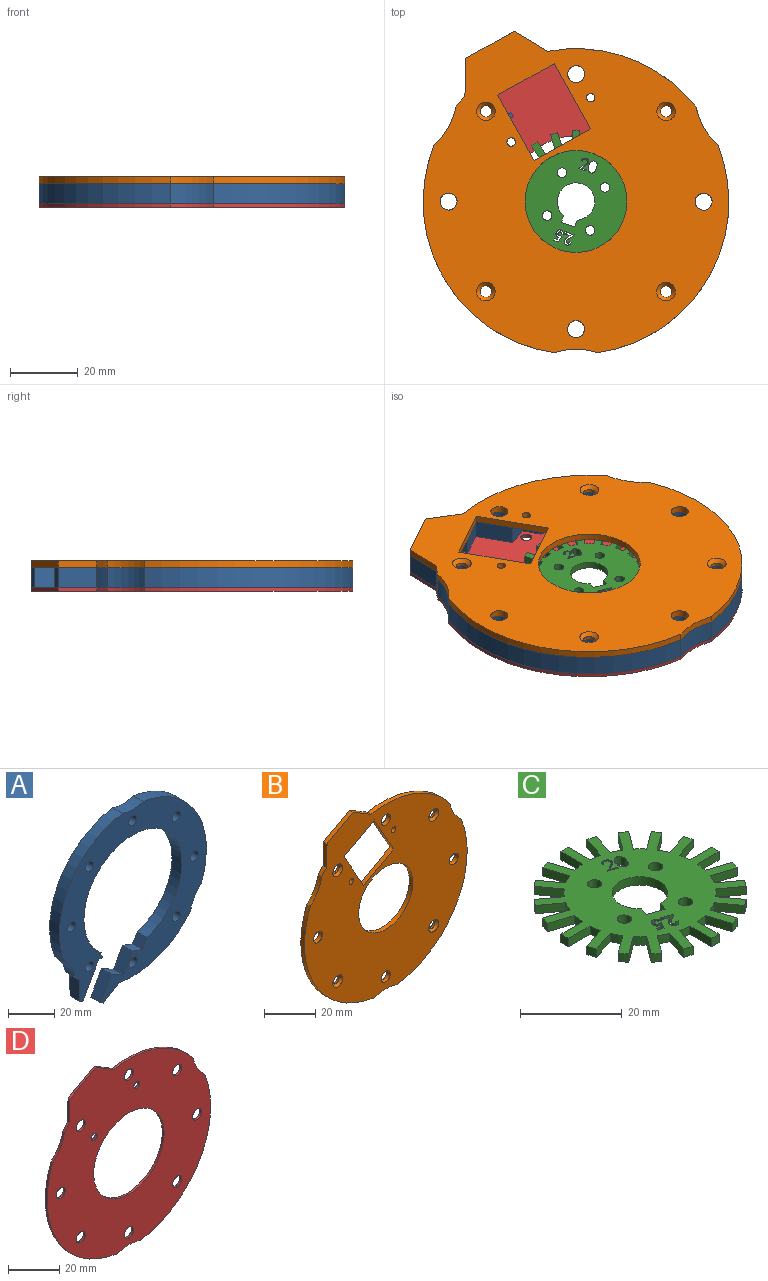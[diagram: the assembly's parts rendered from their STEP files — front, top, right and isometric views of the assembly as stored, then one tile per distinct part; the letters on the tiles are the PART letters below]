
ASSEMBLY  parts=4 mates=5
PART A: 32 faces, bbox 90x6x94.7 mm
  f0: cylinder r=20mm len=11.05mm, axis (0,1,0), area 77.9mm2, adj f1,f21,f22,f23
  f1: cylinder r=45mm len=6mm, axis (0,1,0), area 24.6mm2, adj f0,f2,f22,f23
  f2: plane 11.27x6mm, normal (-1,0,-0.02), area 67.6mm2, adj f1,f3,f22,f23
  f3: plane 6x1.75mm, normal (-0.48,0,-0.88), area 12mm2, adj f2,f4,f22,f23
  f4: plane 17.86x9.86mm, normal (0.88,0,-0.48), area 122.4mm2, adj f3,f5,f22,f23
  f5: plane 6x1.7mm, normal (-0.48,0,-0.88), area 11.6mm2, adj f4,f6,f22,f23
  f6: plane 6x1.23mm, normal (0.88,0,-0.48), area 8.4mm2, adj f5,f7,f22,f23
  f7: plane 6x1.7mm, normal (0.48,0,0.88), area 11.6mm2, adj f6,f8,f22,f23
  f8: plane 6x1.27mm, normal (0.88,0,-0.48), area 8.7mm2, adj f7,f9,f22,f23
  f9: cylinder r=30mm len=60mm, axis (0,1,0), area 951.8mm2, adj f8,f10,f22,f23
  f10: plane 6x4.97mm, normal (-0.88,0,0.48), area 34.1mm2, adj f9,f11,f22,f23
  f11: plane 6.17x6mm, normal (0.34,0,0.94), area 39.5mm2, adj f10,f12,f22,f23
  f12: plane 9.9x6mm, normal (-0.88,0,0.48), area 67.9mm2, adj f11,f13,f22,f23
  f13: plane 7.39x6mm, normal (0.48,0,0.88), area 50.7mm2, adj f12,f14,f22,f23
  f14: plane 11.91x6.57mm, normal (-0.88,0,0.48), area 81.6mm2, adj f13,f15,f22,f23
  f15: plane 6x1.75mm, normal (-0.48,0,-0.88), area 12mm2, adj f14,f16,f22,f23
  f16: plane 9.82x6mm, normal (0.52,0,-0.86), area 68.8mm2, adj f15,f17,f22,f23
  f17: cylinder r=45mm len=43.66mm, axis (0,1,0), area 294.3mm2, adj f16,f18,f22,f23
  f18: cylinder r=20mm len=11.06mm, axis (0,1,0), area 77.9mm2, adj f17,f19,f22,f23
  f19: cylinder r=45mm len=61.26mm, axis (0,1,0), area 488.7mm2, adj f18,f20,f22,f23
  f20: cylinder r=20mm len=12.76mm, axis (0,1,0), area 77.9mm2, adj f19,f21,f22,f23
  f21: cylinder r=45mm len=61.32mm, axis (0,1,0), area 488.7mm2, adj f0,f20,f22,f23
  f22: plane 94.71x90mm, normal (0,-1,0), area 3117.4mm2, adj f0,f1,f2,f3,f4,f5,f6,f7
  f23: plane 94.71x90mm, normal (0,1,0), area 3117.4mm2, adj f0,f1,f2,f3,f4,f5,f6,f7
  f24: cylinder r=2.5mm len=6mm, axis (0,1,0), area 94.2mm2, adj f22,f23
  f25: cylinder r=2.5mm len=6mm, axis (0,1,0), area 94.2mm2, adj f22,f23
  f26: cylinder r=2.5mm len=6mm, axis (0,1,0), area 94.2mm2, adj f22,f23
  f27: cylinder r=2.5mm len=6mm, axis (0,1,0), area 94.2mm2, adj f22,f23
  f28: cylinder r=2.5mm len=6mm, axis (0,1,0), area 94.2mm2, adj f22,f23
  f29: cylinder r=2.5mm len=6mm, axis (0,1,0), area 94.2mm2, adj f22,f23
  f30: cylinder r=2.5mm len=6mm, axis (0,1,0), area 94.2mm2, adj f22,f23
  f31: cylinder r=2.5mm len=6mm, axis (0,1,0), area 94.2mm2, adj f22,f23
PART B: 31 faces, bbox 90x2x94.7 mm
  f0: cylinder r=45mm len=61.29mm, axis (0,1,0), area 162.9mm2, adj f1,f9,f10,f11
  f1: cylinder r=20mm len=11.05mm, axis (0,1,0), area 26mm2, adj f0,f2,f10,f11
  f2: cylinder r=45mm len=43.67mm, axis (0,1,0), area 98.1mm2, adj f1,f3,f10,f11
  f3: plane 9.82x5.91mm, normal (0.52,0,0.86), area 22.9mm2, adj f2,f4,f10,f11
  f4: plane 14.4x7.96mm, normal (-0.48,0,0.88), area 32.9mm2, adj f3,f5,f10,f11
  f5: plane 11.27x2mm, normal (-1,0,0.02), area 22.5mm2, adj f4,f6,f10,f11
  f6: cylinder r=45mm len=3.11mm, axis (0,1,0), area 8.2mm2, adj f5,f7,f10,f11
  f7: cylinder r=20mm len=11.05mm, axis (0,1,0), area 26mm2, adj f6,f8,f10,f11
  f8: cylinder r=45mm len=61.29mm, axis (0,1,0), area 162.9mm2, adj f7,f9,f10,f11
  f9: cylinder r=20mm len=12.76mm, axis (0,1,0), area 26mm2, adj f0,f8,f10,f11
  f10: plane 94.69x90mm, normal (0,-1,0), area 5191.9mm2, adj f0,f1,f2,f3,f4,f5,f6,f7
  f11: plane 94.69x90mm, normal (0,1,0), area 5250.6mm2, adj f0,f1,f2,f3,f4,f5,f6,f7
  f12: cylinder r=15mm len=30mm, axis (0,1,0), area 188.5mm2, adj f10,f11
  f13: cylinder r=1.7mm len=3.4mm, axis (0,1,0), area 10.1mm2, adj f11,f30
  f14: cylinder r=1.7mm len=3.4mm, axis (0,1,0), area 10.1mm2, adj f11,f29
  f15: cylinder r=1.7mm len=3.4mm, axis (0,1,0), area 10.1mm2, adj f11,f28
  f16: cylinder r=2.5mm len=5mm, axis (0,1,0), area 31.4mm2, adj f10,f11
  f17: cylinder r=2.5mm len=5mm, axis (0,1,0), area 31.4mm2, adj f10,f11
  f18: cylinder r=1.7mm len=3.4mm, axis (0,1,0), area 10.1mm2, adj f11,f27
  f19: cylinder r=2.5mm len=5mm, axis (0,1,0), area 31.4mm2, adj f10,f11
  f20: cylinder r=2.5mm len=5mm, axis (0,1,0), area 31.4mm2, adj f10,f11
  f21: cylinder r=1.25mm len=2.5mm, axis (0,1,0), area 15.7mm2, adj f10,f11
  f22: cylinder r=1.25mm len=2.5mm, axis (0,1,0), area 15.7mm2, adj f10,f11
  f23: plane 19.23x10.69mm, normal (0.87,0,0.49), area 44mm2, adj f10,f11,f24,f26
  f24: plane 16.61x9.23mm, normal (-0.49,0,0.87), area 38mm2, adj f10,f11,f23,f25
  f25: plane 19.23x10.69mm, normal (-0.87,0,-0.49), area 44mm2, adj f10,f11,f24,f26
  f26: plane 16.61x9.23mm, normal (0.49,0,-0.87), area 38mm2, adj f10,f11,f23,f25
  f27: cone r=2.75mm half-angle=45deg, axis (0,-1,0), area 20.8mm2, adj f10,f18
  f28: cone r=2.75mm half-angle=45deg, axis (0,-1,0), area 20.8mm2, adj f10,f15
  f29: cone r=2.75mm half-angle=45deg, axis (0,-1,0), area 20.8mm2, adj f10,f14
  f30: cone r=2.75mm half-angle=45deg, axis (0,-1,0), area 20.8mm2, adj f10,f13
PART C: 138 faces, bbox 42x42x2 mm
  f0: plane 42x42mm, normal (0,0,-1), area 813.4mm2, adj f2,f3,f4,f5,f6,f7,f8,f9
  f1: plane 42x42mm, normal (0,0,1), area 813.4mm2, adj f2,f3,f4,f5,f6,f7,f8,f9
  f2: cylinder r=15mm len=2.58mm, axis (0,0,1), area 5.2mm2, adj f0,f1,f32,f87
  f3: cylinder r=15mm len=2.32mm, axis (0,0,1), area 5.2mm2, adj f0,f1,f84,f89
  f4: cylinder r=15mm len=2mm, axis (0,0,1), area 5.2mm2, adj f0,f1,f81,f86
  f5: cylinder r=15mm len=2.32mm, axis (0,0,1), area 5.2mm2, adj f0,f1,f78,f83
  f6: cylinder r=15mm len=2.58mm, axis (0,0,1), area 5.2mm2, adj f0,f1,f75,f80
  f7: cylinder r=15mm len=2.58mm, axis (0,0,1), area 5.2mm2, adj f0,f1,f72,f77
  f8: cylinder r=15mm len=2.32mm, axis (0,0,1), area 5.2mm2, adj f0,f1,f69,f74
  f9: cylinder r=15mm len=2mm, axis (0,0,1), area 5.2mm2, adj f0,f1,f66,f71
  f10: cylinder r=15mm len=2.32mm, axis (0,0,1), area 5.2mm2, adj f0,f1,f63,f68
  f11: cylinder r=15mm len=2.58mm, axis (0,0,1), area 5.2mm2, adj f0,f1,f60,f65
  f12: cylinder r=15mm len=2.58mm, axis (0,0,1), area 5.2mm2, adj f0,f1,f57,f62
  f13: cylinder r=15mm len=2.32mm, axis (0,0,1), area 5.2mm2, adj f0,f1,f54,f59
  f14: cylinder r=15mm len=2mm, axis (0,0,1), area 5.2mm2, adj f0,f1,f51,f56
  f15: cylinder r=15mm len=2.32mm, axis (0,0,1), area 5.2mm2, adj f0,f1,f48,f53
  f16: cylinder r=15mm len=2.58mm, axis (0,0,1), area 5.2mm2, adj f0,f1,f45,f50
  f17: cylinder r=15mm len=2.58mm, axis (0,0,1), area 5.2mm2, adj f0,f1,f42,f47
  f18: cylinder r=15mm len=2.32mm, axis (0,0,1), area 5.2mm2, adj f0,f1,f39,f44
  f19: cylinder r=15mm len=2mm, axis (0,0,1), area 5.2mm2, adj f0,f1,f36,f41
  f20: cylinder r=15mm len=2.32mm, axis (0,0,1), area 5.2mm2, adj f0,f1,f33,f38
  f21: cylinder r=15mm len=2.58mm, axis (0,0,1), area 5.2mm2, adj f0,f1,f30,f35
  f22: cylinder r=5.5mm len=11mm, axis (0,0,1), area 60.5mm2, adj f0,f1,f23,f25
  f23: plane 2x2mm, normal (-0.95,0.33,0), area 4.2mm2, adj f0,f1,f22,f24
  f24: plane 3.97x2mm, normal (0.33,0.95,0), area 8.4mm2, adj f0,f1,f23,f25
  f25: plane 2x2mm, normal (0.95,-0.33,0), area 4.2mm2, adj f0,f1,f22,f24
  f26: cylinder r=1.4mm len=2.8mm, axis (0,0,1), area 17.6mm2, adj f0,f1
  f27: cylinder r=1.4mm len=2.8mm, axis (0,0,1), area 17.6mm2, adj f0,f1
  f28: cylinder r=1.4mm len=2.8mm, axis (0,0,1), area 17.6mm2, adj f0,f1
  f29: cylinder r=1.4mm len=2.8mm, axis (0,0,1), area 17.6mm2, adj f0,f1
  f30: plane 6.01x2mm, normal (-1,0,0), area 12mm2, adj f0,f1,f21,f31
  f31: cylinder r=21mm len=2.1mm, axis (0,0,1), area 4.2mm2, adj f0,f1,f30,f32
  f32: plane 6.01x2mm, normal (1,0,0), area 12mm2, adj f0,f1,f2,f31
  f33: plane 5.72x2mm, normal (-0.95,-0.31,0), area 12mm2, adj f0,f1,f20,f34
  f34: cylinder r=21mm len=2mm, axis (0,0,1), area 4.2mm2, adj f0,f1,f33,f35
  f35: plane 5.72x2mm, normal (0.95,0.31,0), area 12mm2, adj f0,f1,f21,f34
  f36: plane 4.86x3.53mm, normal (-0.81,-0.59,0), area 12mm2, adj f0,f1,f19,f37
  f37: cylinder r=21mm len=2mm, axis (0,0,1), area 4.2mm2, adj f0,f1,f36,f38
  f38: plane 4.86x3.53mm, normal (0.81,0.59,0), area 12mm2, adj f0,f1,f20,f37
  f39: plane 4.86x3.53mm, normal (-0.59,-0.81,0), area 12mm2, adj f0,f1,f18,f40
  f40: cylinder r=21mm len=2mm, axis (0,0,1), area 4.2mm2, adj f0,f1,f39,f41
  f41: plane 4.86x3.53mm, normal (0.59,0.81,0), area 12mm2, adj f0,f1,f19,f40
  f42: plane 5.72x2mm, normal (-0.31,-0.95,0), area 12mm2, adj f0,f1,f17,f43
  f43: cylinder r=21mm len=2mm, axis (0,0,1), area 4.2mm2, adj f0,f1,f42,f44
  f44: plane 5.72x2mm, normal (0.31,0.95,0), area 12mm2, adj f0,f1,f18,f43
  f45: plane 6.01x2mm, normal (0,-1,0), area 12mm2, adj f0,f1,f16,f46
  f46: cylinder r=21mm len=2.1mm, axis (0,0,1), area 4.2mm2, adj f0,f1,f45,f47
  f47: plane 6.01x2mm, normal (0,1,0), area 12mm2, adj f0,f1,f17,f46
  f48: plane 5.72x2mm, normal (0.31,-0.95,0), area 12mm2, adj f0,f1,f15,f49
  f49: cylinder r=21mm len=2mm, axis (0,0,1), area 4.2mm2, adj f0,f1,f48,f50
  f50: plane 5.72x2mm, normal (-0.31,0.95,0), area 12mm2, adj f0,f1,f16,f49
  f51: plane 4.86x3.53mm, normal (0.59,-0.81,0), area 12mm2, adj f0,f1,f14,f52
  f52: cylinder r=21mm len=2mm, axis (0,0,1), area 4.2mm2, adj f0,f1,f51,f53
  f53: plane 4.86x3.53mm, normal (-0.59,0.81,0), area 12mm2, adj f0,f1,f15,f52
  f54: plane 4.86x3.53mm, normal (0.81,-0.59,0), area 12mm2, adj f0,f1,f13,f55
  f55: cylinder r=21mm len=2mm, axis (0,0,1), area 4.2mm2, adj f0,f1,f54,f56
  f56: plane 4.86x3.53mm, normal (-0.81,0.59,0), area 12mm2, adj f0,f1,f14,f55
  f57: plane 5.72x2mm, normal (0.95,-0.31,0), area 12mm2, adj f0,f1,f12,f58
  f58: cylinder r=21mm len=2mm, axis (0,0,1), area 4.2mm2, adj f0,f1,f57,f59
  f59: plane 5.72x2mm, normal (-0.95,0.31,0), area 12mm2, adj f0,f1,f13,f58
  f60: plane 6.01x2mm, normal (1,0,0), area 12mm2, adj f0,f1,f11,f61
  f61: cylinder r=21mm len=2.1mm, axis (0,0,1), area 4.2mm2, adj f0,f1,f60,f62
  f62: plane 6.01x2mm, normal (-1,0,0), area 12mm2, adj f0,f1,f12,f61
  f63: plane 5.72x2mm, normal (0.95,0.31,0), area 12mm2, adj f0,f1,f10,f64
  f64: cylinder r=21mm len=2mm, axis (0,0,1), area 4.2mm2, adj f0,f1,f63,f65
  f65: plane 5.72x2mm, normal (-0.95,-0.31,0), area 12mm2, adj f0,f1,f11,f64
  f66: plane 4.86x3.53mm, normal (0.81,0.59,0), area 12mm2, adj f0,f1,f9,f67
  f67: cylinder r=21mm len=2mm, axis (0,0,1), area 4.2mm2, adj f0,f1,f66,f68
  f68: plane 4.86x3.53mm, normal (-0.81,-0.59,0), area 12mm2, adj f0,f1,f10,f67
  f69: plane 4.86x3.53mm, normal (0.59,0.81,0), area 12mm2, adj f0,f1,f8,f70
  f70: cylinder r=21mm len=2mm, axis (0,0,1), area 4.2mm2, adj f0,f1,f69,f71
  f71: plane 4.86x3.53mm, normal (-0.59,-0.81,0), area 12mm2, adj f0,f1,f9,f70
  f72: plane 5.72x2mm, normal (0.31,0.95,0), area 12mm2, adj f0,f1,f7,f73
  f73: cylinder r=21mm len=2mm, axis (0,0,1), area 4.2mm2, adj f0,f1,f72,f74
  f74: plane 5.72x2mm, normal (-0.31,-0.95,0), area 12mm2, adj f0,f1,f8,f73
  f75: plane 6.01x2mm, normal (0,1,0), area 12mm2, adj f0,f1,f6,f76
  f76: cylinder r=21mm len=2.1mm, axis (0,0,1), area 4.2mm2, adj f0,f1,f75,f77
  f77: plane 6.01x2mm, normal (0,-1,0), area 12mm2, adj f0,f1,f7,f76
  f78: plane 5.72x2mm, normal (-0.31,0.95,0), area 12mm2, adj f0,f1,f5,f79
  f79: cylinder r=21mm len=2mm, axis (0,0,1), area 4.2mm2, adj f0,f1,f78,f80
  f80: plane 5.72x2mm, normal (0.31,-0.95,0), area 12mm2, adj f0,f1,f6,f79
  f81: plane 4.86x3.53mm, normal (-0.59,0.81,0), area 12mm2, adj f0,f1,f4,f82
  f82: cylinder r=21mm len=2mm, axis (0,0,1), area 4.2mm2, adj f0,f1,f81,f83
  f83: plane 4.86x3.53mm, normal (0.59,-0.81,0), area 12mm2, adj f0,f1,f5,f82
  f84: plane 4.86x3.53mm, normal (-0.81,0.59,0), area 12mm2, adj f0,f1,f3,f85
  f85: cylinder r=21mm len=2mm, axis (0,0,1), area 4.2mm2, adj f0,f1,f84,f86
  f86: plane 4.86x3.53mm, normal (0.81,-0.59,0), area 12mm2, adj f0,f1,f4,f85
  f87: plane 5.72x2mm, normal (-0.95,0.31,0), area 12mm2, adj f0,f1,f2,f88
  f88: cylinder r=21mm len=2mm, axis (0,0,1), area 4.2mm2, adj f0,f1,f87,f89
  f89: plane 5.72x2mm, normal (0.95,-0.31,0), area 12mm2, adj f0,f1,f3,f88
  f90: extruded ~2x1.04mm, area 2.6mm2, adj f0,f1,f91,f101
  f91: plane 2x0.32mm, normal (0.33,0.95,0), area 0.7mm2, adj f0,f1,f90,f92
  f92: extruded ~2x1.48mm, area 3.7mm2, adj f0,f1,f91,f93
  f93: extruded ~2x1.33mm, area 3.3mm2, adj f0,f1,f92,f94
  f94: extruded ~2x1.06mm, area 2.9mm2, adj f0,f1,f93,f95
  f95: plane 2x1.12mm, normal (-0.47,0.88,0), area 2.5mm2, adj f0,f1,f94,f96
  f96: plane 2x1.52mm, normal (-0.33,-0.95,0), area 3.2mm2, adj f0,f1,f95,f97
  f97: plane 2x0.32mm, normal (-0.95,0.33,0), area 0.7mm2, adj f0,f1,f96,f98
  f98: plane 2.23x2mm, normal (0.33,0.95,0), area 4.7mm2, adj f0,f1,f97,f99
  f99: plane 2x1.72mm, normal (0.47,-0.88,0), area 3.9mm2, adj f0,f1,f98,f100
  f100: extruded ~2x0.96mm, area 2.6mm2, adj f0,f1,f99,f101
  f101: extruded ~2x0.92mm, area 2.3mm2, adj f0,f1,f90,f100
  f102: extruded ~2x0.43mm, area 1.1mm2, adj f0,f1,f103,f105
  f103: extruded ~2x0.46mm, area 1.1mm2, adj f0,f1,f102,f104
  f104: extruded ~2x0.43mm, area 1.1mm2, adj f0,f1,f103,f105
  f105: extruded ~2x0.46mm, area 1.1mm2, adj f0,f1,f102,f104
  f106: extruded ~2x0.61mm, area 1.6mm2, adj f0,f1,f107,f118
  f107: plane 2x0.54mm, normal (-0.33,-0.95,0), area 1.1mm2, adj f0,f1,f106,f108
  f108: extruded ~2x1.39mm, area 3.6mm2, adj f0,f1,f107,f109
  f109: extruded ~2x1.29mm, area 3.1mm2, adj f0,f1,f108,f110
  f110: extruded ~2x1.19mm, area 3.4mm2, adj f0,f1,f109,f111
  f111: plane 2x0.46mm, normal (0.52,-0.86,0), area 1.1mm2, adj f0,f1,f110,f112
  f112: plane 2x1.03mm, normal (0.33,0.95,0), area 2.2mm2, adj f0,f1,f111,f113
  f113: plane 2x0.58mm, normal (0.95,-0.33,0), area 1.2mm2, adj f0,f1,f112,f114
  f114: plane 2.01x2mm, normal (-0.33,-0.95,0), area 4.3mm2, adj f0,f1,f113,f115
  f115: plane 2x0.3mm, normal (-0.95,0.33,0), area 0.6mm2, adj f0,f1,f114,f116
  f116: plane 2x1.25mm, normal (-0.5,0.86,0), area 2.9mm2, adj f0,f1,f115,f117
  f117: extruded ~2x0.89mm, area 2.5mm2, adj f0,f1,f116,f118
  f118: extruded ~2x0.58mm, area 1.4mm2, adj f0,f1,f106,f117
  f119: plane 2x1.71mm, normal (-0.87,0.5,0), area 3.9mm2, adj f0,f1,f120,f133
  f120: plane 2x1.36mm, normal (0.33,0.95,0), area 2.9mm2, adj f0,f1,f119,f121
  f121: plane 2x0.58mm, normal (0.95,-0.33,0), area 1.2mm2, adj f0,f1,f120,f122
  f122: plane 2x0.95mm, normal (-0.33,-0.95,0), area 2mm2, adj f0,f1,f121,f123
  f123: plane 2x0.56mm, normal (0.86,-0.5,0), area 1.3mm2, adj f0,f1,f122,f124
  f124: cylinder r=0.69mm len=2mm, axis (0,0,-1), area 0.4mm2, adj f0,f1,f123,f125
  f125: extruded ~2x1.4mm, area 3.4mm2, adj f0,f1,f124,f126
  f126: extruded ~2x1.38mm, area 3.6mm2, adj f0,f1,f125,f127
  f127: extruded ~2x1.23mm, area 3.1mm2, adj f0,f1,f126,f128
  f128: plane 2x0.58mm, normal (0.33,0.95,0), area 1.2mm2, adj f0,f1,f127,f129
  f129: extruded ~2x0.46mm, area 1.2mm2, adj f0,f1,f128,f130
  f130: extruded ~2x0.62mm, area 1.6mm2, adj f0,f1,f129,f131
  f131: extruded ~2x0.66mm, area 1.6mm2, adj f0,f1,f130,f132
  f132: extruded ~2x0.42mm, area 0.9mm2, adj f0,f1,f131,f133
  f133: plane 2x0.41mm, normal (-0.55,-0.84,0), area 1mm2, adj f0,f1,f119,f132
  f134: extruded ~2.11x2mm, area 4.9mm2, adj f0,f1,f135,f137
  f135: extruded ~2x1.7mm, area 4.9mm2, adj f0,f1,f134,f136
  f136: extruded ~2.12x2mm, area 4.9mm2, adj f0,f1,f135,f137
  f137: extruded ~2x1.73mm, area 4.9mm2, adj f0,f1,f134,f136
PART D: 23 faces, bbox 90x1x94.7 mm
  f0: cylinder r=45mm len=61.29mm, axis (0,1,0), area 81.4mm2, adj f1,f9,f10,f11
  f1: cylinder r=20mm len=11.05mm, axis (0,1,0), area 13mm2, adj f0,f2,f10,f11
  f2: cylinder r=45mm len=43.67mm, axis (0,1,0), area 49.1mm2, adj f1,f3,f10,f11
  f3: plane 9.82x5.91mm, normal (0.52,0,0.86), area 11.5mm2, adj f2,f4,f10,f11
  f4: plane 14.4x7.96mm, normal (-0.48,0,0.88), area 16.5mm2, adj f3,f5,f10,f11
  f5: plane 11.27x1mm, normal (-1,0,0.02), area 11.3mm2, adj f4,f6,f10,f11
  f6: cylinder r=45mm len=3.11mm, axis (0,1,0), area 4.1mm2, adj f5,f7,f10,f11
  f7: cylinder r=20mm len=11.05mm, axis (0,1,0), area 13mm2, adj f6,f8,f10,f11
  f8: cylinder r=45mm len=61.29mm, axis (0,1,0), area 81.4mm2, adj f7,f9,f10,f11
  f9: cylinder r=20mm len=12.76mm, axis (0,1,0), area 13mm2, adj f0,f8,f10,f11
  f10: plane 94.69x90mm, normal (0,-1,0), area 5147.7mm2, adj f0,f1,f2,f3,f4,f5,f6,f7
  f11: plane 94.69x90mm, normal (0,1,0), area 5147.7mm2, adj f0,f1,f2,f3,f4,f5,f6,f7
  f12: cylinder r=19.37mm len=38.75mm, axis (0,1,0), area 121.7mm2, adj f10,f11
  f13: cylinder r=2.5mm len=5mm, axis (0,1,0), area 15.7mm2, adj f10,f11
  f14: cylinder r=2.5mm len=5mm, axis (0,1,0), area 15.7mm2, adj f10,f11
  f15: cylinder r=2.5mm len=5mm, axis (0,1,0), area 15.7mm2, adj f10,f11
  f16: cylinder r=2.5mm len=5mm, axis (0,1,0), area 15.7mm2, adj f10,f11
  f17: cylinder r=2.5mm len=5mm, axis (0,1,0), area 15.7mm2, adj f10,f11
  f18: cylinder r=2.5mm len=5mm, axis (0,1,0), area 15.7mm2, adj f10,f11
  f19: cylinder r=2.5mm len=5mm, axis (0,1,0), area 15.7mm2, adj f10,f11
  f20: cylinder r=2.5mm len=5mm, axis (0,1,0), area 15.7mm2, adj f10,f11
  f21: cylinder r=1.6mm len=3.2mm, axis (0,1,0), area 10.1mm2, adj f10,f11
  f22: cylinder r=1.6mm len=3.2mm, axis (0,1,0), area 10.1mm2, adj f10,f11
PLACE A rot(axis=(1,0,0),90deg) t=(0.03,-0.05,-2)mm
PLACE B rot(axis=(-1,0,0),90deg) t=(0,0,-2)mm
PLACE C rot(axis=(0,0,1),0deg) t=(0,0,-3.43)mm
PLACE D rot(axis=(-1,0,0),90deg) t=(0,0,-9)mm
MATE slider A.f1 <-> B.f0  axis (0,0,1) through (0,0,-5)mm
MATE planar A.f22 <-> D.f10  axis (0,0,-1) through (0.65,-2.14,-8)mm
MATE planar A.f23 <-> B.f11  axis (0,0,1) through (0.65,-2.14,-2)mm
MATE slider D.f0 <-> A.f1  axis (0,0,-1) through (0,0,-8.5)mm
MATE slider C.f2 <-> A.f1  axis (0,0,1) through (0,0,-4.43)mm
